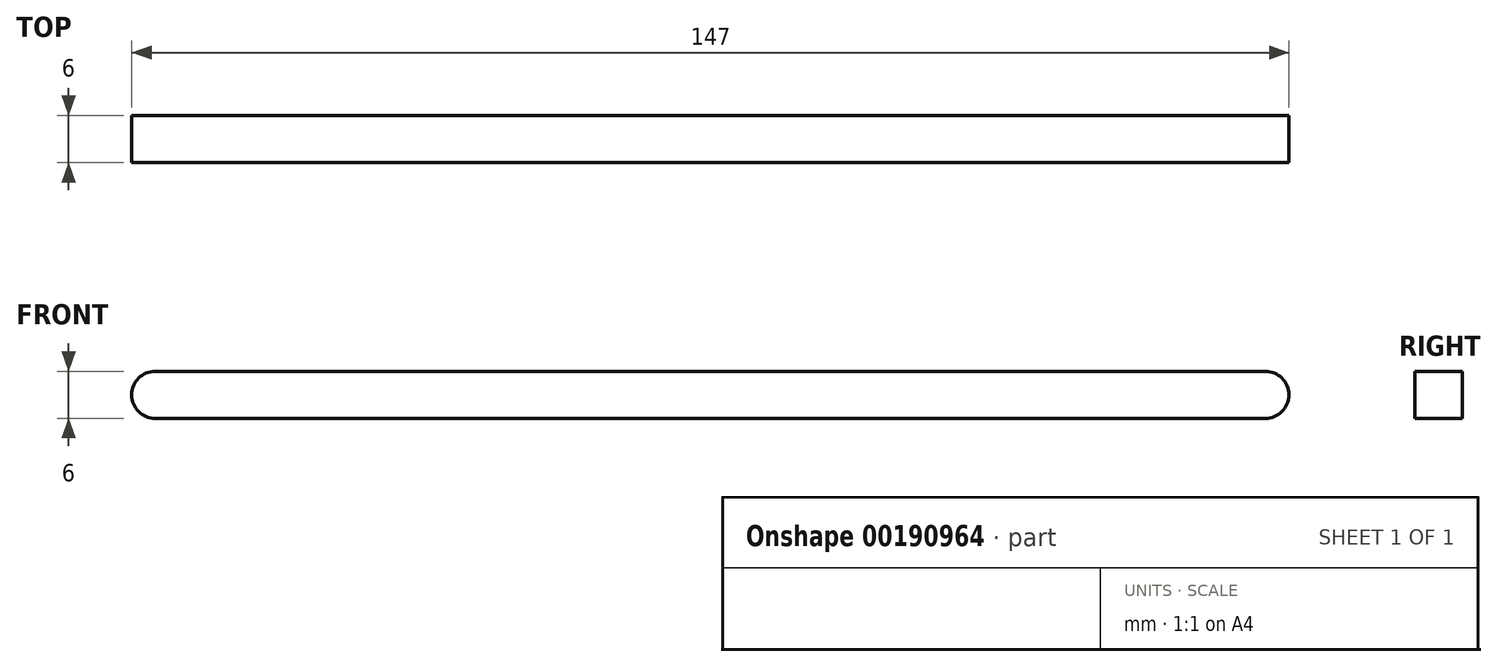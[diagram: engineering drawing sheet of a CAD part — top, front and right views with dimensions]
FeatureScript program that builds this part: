
annotation { "Feature Type Name" : "Feature", "Feature Type Description" : "" }
export const myFeature = defineFeature(function(context is Context, id is Id, definition is map)
    precondition{}
    {
        {
            var Q0;
            Q0=qCreatedBy(makeId("Front.planeOp"),FACE);
            var sketch = newSketch(context, id + "F0", { "sketchPlane" : qUnion([Q0])});
            skLineSegment(sketch, "E0.bottom", {"start": v(0, 0) * mm, "end": v(141, 0) * mm});
            skLineSegment(sketch, "E0.top", {"start": v(0, 6) * mm, "end": v(141, 6) * mm});
            skLineSegment(sketch, "E0.left", {"start": v(0, 0) * mm, "end": v(0, 6) * mm});
            skLineSegment(sketch, "E0.right", {"start": v(141, 0) * mm, "end": v(141, 6) * mm});
            skArc(sketch, "E1", {"start": v(141, 6) * mm, "mid": v(144, 3) * mm, "end": v(141, 0) * mm});
            skArc(sketch, "E2", {"start": v(0, 0) * mm, "mid": v(-3, 3) * mm, "end": v(0, 6) * mm});
            skLineSegment(sketch, "E3", {"start": v(-3, 3) * mm, "end": v(144, 3) * mm, "construction": true});
            skSolve(sketch);
        }
        {
            var Q0;
            Q0=makeQuery(id+"F0.imprint","IMPRINT",FACE,{"disambiguationData":[TD([[makeQuery(id+"F0.imprint","IMPRINT",EDGE,{"derivedFrom":sQuery(id+"F0.wireOp",EDGE,"E0.bottom")}),1.0]])]});
            var Q1;
            Q1=makeQuery(id+"F0.imprint","IMPRINT",FACE,{"disambiguationData":[TD([[makeQuery(id+"F0.imprint","IMPRINT",EDGE,{"derivedFrom":sQuery(id+"F0.wireOp",EDGE,"E0.right")}),-1.0]])]});
            var Q2;
            Q2=makeQuery(id+"F0.imprint","IMPRINT",FACE,{"disambiguationData":[TD([[makeQuery(id+"F0.imprint","IMPRINT",EDGE,{"derivedFrom":sQuery(id+"F0.wireOp",EDGE,"E0.left")}),1.0]])]});
            extrude(context, id + "F1", {"entities" : qUnion([Q0, Q1, Q2]), "depth" : 6 * mm});
        }
    });
